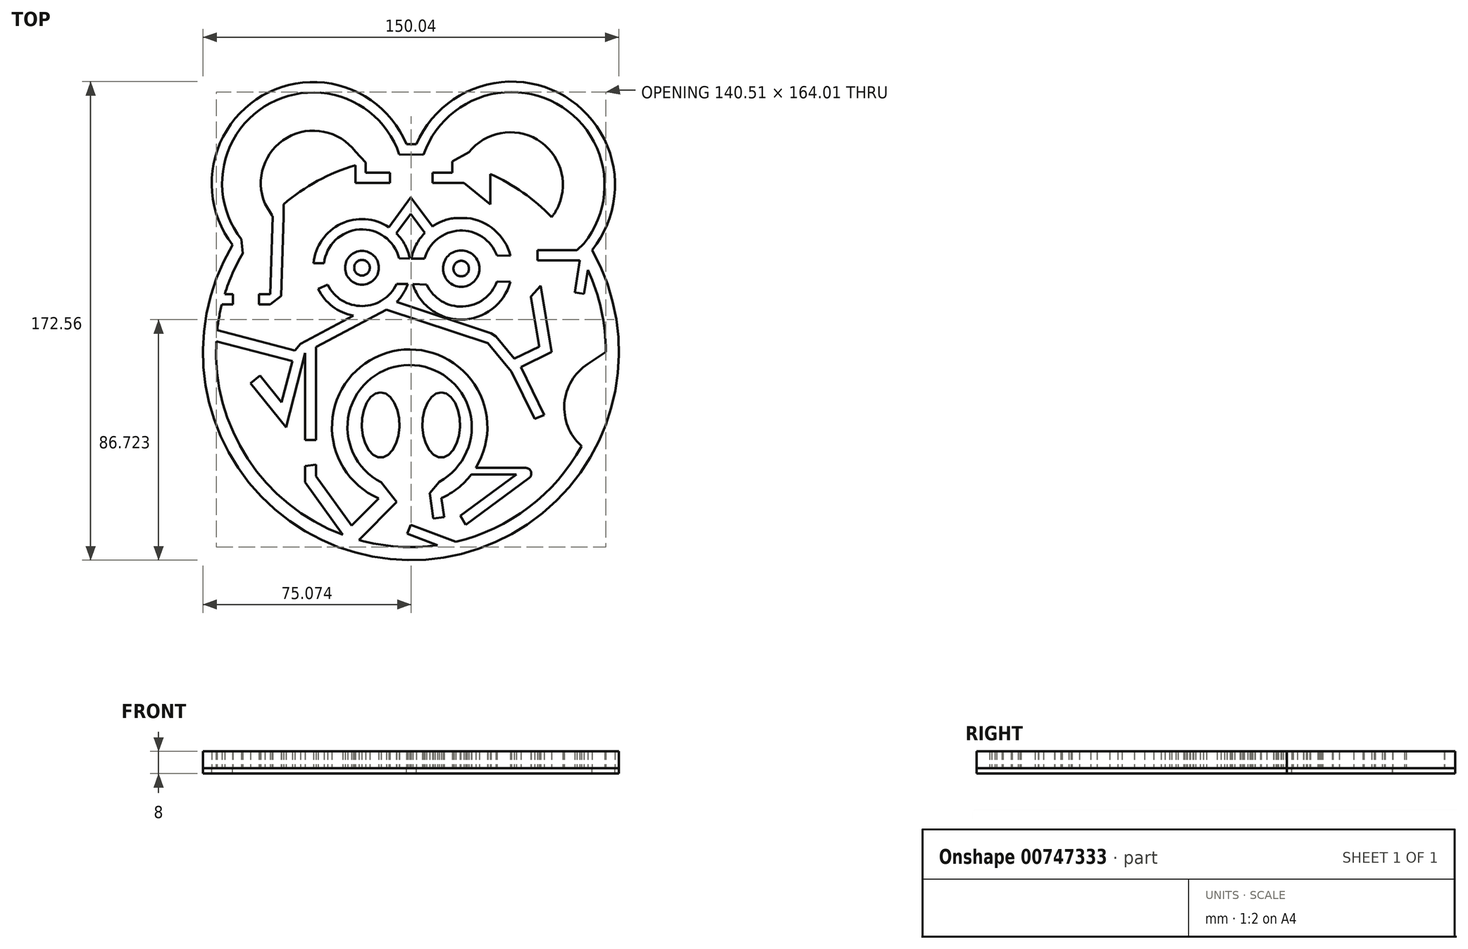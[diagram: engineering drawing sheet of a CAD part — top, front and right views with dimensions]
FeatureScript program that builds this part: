
annotation { "Feature Type Name" : "Feature", "Feature Type Description" : "" }
export const myFeature = defineFeature(function(context is Context, id is Id, definition is map)
    precondition{}
    {
        {
            var Q0;
            Q0=qCreatedBy(makeId("Top.planeOp"),FACE);
            var sketch = newSketch(context, id + "F0", { "sketchPlane" : qUnion([Q0])});
            skArc(sketch, "E0", {"start": v(-64.31, 38.62) * mm, "mid": v(-1.05, -75) * mm, "end": v(65.36, 36.81) * mm});
            skArc(sketch, "E1.0", {"start": v(-68.18, 17.17) * mm, "mid": v(-69.18, 12.55) * mm, "end": v(-69.87, 7.88) * mm});
            skArc(sketch, "E2", {"start": v(-50.1, 94.24) * mm, "mid": v(-70.69, 69.88) * mm, "end": v(-64.31, 38.62) * mm});
            skArc(sketch, "E3", {"start": v(-50.1, 94.24) * mm, "mid": v(-21.8, 94.8) * mm, "end": v(-1.58, 75) * mm});
            skArc(sketch, "E4", {"start": v(53.87, 93.14) * mm, "mid": v(72.86, 67.68) * mm, "end": v(65.36, 36.81) * mm});
            skArc(sketch, "E5", {"start": v(53.87, 93.14) * mm, "mid": v(23.96, 95.45) * mm, "end": v(2.02, 74.99) * mm});
            skArc(sketch, "E6.0", {"start": v(10.18, -46.8) * mm, "mid": v(-0.63, -4.68) * mm, "end": v(-10.76, -46.97) * mm});
            skArc(sketch, "E7.0", {"start": v(53.27, 52.82) * mm, "mid": v(52.03, 50.46) * mm, "end": v(50.46, 48.3) * mm});
            skArc(sketch, "E8", {"start": v(-30, 24.26) * mm, "mid": v(-17.5, 16.6) * mm, "end": v(-5.15, 24.5) * mm});
            skArc(sketch, "E9", {"start": v(5.71, 24.34) * mm, "mid": v(18.76, 16.41) * mm, "end": v(31.05, 25.48) * mm});
            skCircle(sketch, "E10", {"center": v(-17.64, 30.41) * mm, "radius": 6.08 * mm});
            skCircle(sketch, "E11", {"center": v(18.15, 30.11) * mm, "radius": 6.56 * mm});
            skLineSegment(sketch, "E12.trimOffspring", {"start": v(-49.84, 48.88) * mm, "end": v(-50.05, 49.39) * mm, "construction": true});
            skLineSegment(sketch, "E13.trimOffspring", {"start": v(50.46, 48.3) * mm, "end": v(50.66, 48.76) * mm, "construction": true});
            skArc(sketch, "E14.0", {"start": v(-5.2, 18.03) * mm, "mid": v(-2.8, 21.04) * mm, "end": v(-1.1, 24.5) * mm});
            skArc(sketch, "E15.0", {"start": v(15.62, 48.31) * mm, "mid": v(5.54, 43.48) * mm, "end": v(0.12, 33.71) * mm});
            skCircle(sketch, "E16.0", {"center": v(18.15, 30.11) * mm, "radius": 2.81 * mm});
            skCircle(sketch, "E17.0", {"center": v(-17.64, 30.41) * mm, "radius": 2.81 * mm});
            skEllipse(sketch, "E18", {"center": v(-10.95, -26.25) * mm, "majorRadius": 11.74 * mm, "minorRadius": 6.8 * mm, "majorAxis": v(0, 1)});
            skEllipse(sketch, "E19.MirrorC", {"center": v(10.95, -26.25) * mm, "majorRadius": 11.74 * mm, "minorRadius": 6.8 * mm, "majorAxis": v(0, 1)});
            skArc(sketch, "E20.0", {"start": v(11.04, -52.64) * mm, "mid": v(16.92, -49.08) * mm, "end": v(21.75, -44.2) * mm});
            skFitSpline(sketch, "E21.0", {"points": [v(-10.29, -16.58) * mm, v(-10.95, -16.47) * mm, v(-11.6, -16.58) * mm, v(-12.24, -16.9) * mm, v(-12.79, -17.34) * mm, v(-13.35, -17.92) * mm, v(-14.04, -18.89) * mm, v(-14.76, -20.4) * mm, v(-15.31, -22.2) * mm, v(-15.6, -23.84) * mm, v(-15.72, -25.2) * mm, v(-15.75, -26.25) * mm, v(-15.72, -27.3) * mm, v(-15.6, -28.66) * mm, v(-15.31, -30.3) * mm, v(-14.76, -32.1) * mm, v(-14.04, -33.61) * mm, v(-13.35, -34.58) * mm, v(-12.79, -35.16) * mm, v(-12.24, -35.6) * mm, v(-11.6, -35.92) * mm, v(-10.95, -36.03) * mm, v(-10.29, -35.92) * mm, v(-9.65, -35.6) * mm, v(-9.1, -35.16) * mm, v(-8.54, -34.58) * mm, v(-7.85, -33.61) * mm, v(-7.14, -32.1) * mm, v(-6.58, -30.3) * mm, v(-6.29, -28.66) * mm, v(-6.17, -27.3) * mm, v(-6.14, -26.25) * mm, v(-6.17, -25.2) * mm, v(-6.29, -23.84) * mm, v(-6.58, -22.2) * mm, v(-7.14, -20.4) * mm, v(-7.85, -18.89) * mm, v(-8.54, -17.92) * mm, v(-9.1, -17.34) * mm, v(-9.65, -16.9) * mm, v(-10.29, -16.58) * mm, v(-10.95, -16.47) * mm, v(-11.6, -16.58) * mm, v(-10.29, -16.58) * mm]});
            skFitSpline(sketch, "E22.0", {"points": [v(11.6, -16.58) * mm, v(10.95, -16.47) * mm, v(10.29, -16.58) * mm, v(9.65, -16.9) * mm, v(9.1, -17.34) * mm, v(8.54, -17.92) * mm, v(7.85, -18.89) * mm, v(7.14, -20.4) * mm, v(6.58, -22.2) * mm, v(6.29, -23.84) * mm, v(6.17, -25.2) * mm, v(6.14, -26.25) * mm, v(6.17, -27.3) * mm, v(6.29, -28.66) * mm, v(6.58, -30.3) * mm, v(7.14, -32.1) * mm, v(7.85, -33.61) * mm, v(8.54, -34.58) * mm, v(9.1, -35.16) * mm, v(9.65, -35.6) * mm, v(10.29, -35.92) * mm, v(10.95, -36.03) * mm, v(11.6, -35.92) * mm, v(12.24, -35.6) * mm, v(12.79, -35.16) * mm, v(13.35, -34.58) * mm, v(14.04, -33.61) * mm, v(14.76, -32.1) * mm, v(15.31, -30.3) * mm, v(15.6, -28.66) * mm, v(15.72, -27.3) * mm, v(15.75, -26.25) * mm, v(15.72, -25.2) * mm, v(15.6, -23.84) * mm, v(15.31, -22.2) * mm, v(14.76, -20.4) * mm, v(14.04, -18.89) * mm, v(13.35, -17.92) * mm, v(12.79, -17.34) * mm, v(12.24, -16.9) * mm, v(11.6, -16.58) * mm, v(10.95, -16.47) * mm, v(10.29, -16.58) * mm, v(11.6, -16.58) * mm]});
            skLineSegment(sketch, "E23.bottom", {"start": v(10.1, -46.8) * mm, "end": v(10.18, -46.8) * mm, "construction": true});
            skLineSegment(sketch, "E24", {"start": v(-69.87, 7.88) * mm, "end": v(-41.79, 0.6) * mm});
            skLineSegment(sketch, "E25", {"start": v(-38.15, -0.33) * mm, "end": v(-45.08, -27.08) * mm});
            skLineSegment(sketch, "E26", {"start": v(-45.08, -27.08) * mm, "end": v(-57.79, -11.22) * mm});
            skLineSegment(sketch, "E27", {"start": v(-38.15, -46.97) * mm, "end": v(-38.15, -41.04) * mm});
            skLineSegment(sketch, "E28", {"start": v(-38.15, -46.97) * mm, "end": v(-24.58, -65.87) * mm});
            skLineSegment(sketch, "E29", {"start": v(-21.35, -62.6) * mm, "end": v(-11.67, -52.77) * mm});
            skLineSegment(sketch, "E30", {"start": v(-67.14, 20.87) * mm, "end": v(-64.16, 20.87) * mm});
            skLineSegment(sketch, "E31", {"start": v(-50.77, 20.87) * mm, "end": v(-49.84, 48.88) * mm});
            skLineSegment(sketch, "E32", {"start": v(15.62, 48.31) * mm, "end": v(20.3, 48.36) * mm});
            skLineSegment(sketch, "E33", {"start": v(50.81, 0) * mm, "end": v(39.66, -5.46) * mm});
            skLineSegment(sketch, "E34", {"start": v(36.3, -7.11) * mm, "end": v(27.77, 3.17) * mm});
            skLineSegment(sketch, "E35", {"start": v(27.77, 3.17) * mm, "end": v(16.64, 6.84) * mm});
            skLineSegment(sketch, "E36", {"start": v(-8.8, 15.25) * mm, "end": v(-34.18, 1.78) * mm});
            skLineSegment(sketch, "E37", {"start": v(36.3, -7.11) * mm, "end": v(44.6, -24.08) * mm});
            skLineSegment(sketch, "E38", {"start": v(23.4, -41.79) * mm, "end": v(41.4, -41.79) * mm});
            skLineSegment(sketch, "E39", {"start": v(38, -44.18) * mm, "end": v(27.01, -52.25) * mm});
            skLineSegment(sketch, "E40", {"start": v(11.04, -52.64) * mm, "end": v(11.99, -59.47) * mm});
            skLineSegment(sketch, "E41.0", {"start": v(-46.83, 20.25) * mm, "end": v(-45.89, 48.85) * mm});
            skLineSegment(sketch, "E42.0", {"start": v(-70.76, 4.05) * mm, "end": v(-42.77, -3.2) * mm});
            skLineSegment(sketch, "E43.0", {"start": v(-46.65, -18.17) * mm, "end": v(-54.4, -8.5) * mm});
            skLineSegment(sketch, "E44.0", {"start": v(-42.77, -3.2) * mm, "end": v(-46.65, -18.17) * mm});
            skLineSegment(sketch, "E45.0", {"start": v(-34.18, -44.73) * mm, "end": v(-34.18, -40.57) * mm});
            skLineSegment(sketch, "E46.0", {"start": v(-18.7, -67.78) * mm, "end": v(-5.16, -54.03) * mm});
            skLineSegment(sketch, "E47.0", {"start": v(6.84, -50.86) * mm, "end": v(8.1, -60) * mm});
            skLineSegment(sketch, "E48.0", {"start": v(42.6, -45.44) * mm, "end": v(29.24, -55.28) * mm});
            skLineSegment(sketch, "E49.0", {"start": v(28.94, 6.75) * mm, "end": v(18.03, 10.36) * mm});
            skLineSegment(sketch, "E50.0", {"start": v(-10.5, 18.57) * mm, "end": v(-11.68, 17.95) * mm});
            skLineSegment(sketch, "E51.0", {"start": v(37.34, -2.43) * mm, "end": v(30.68, 5.6) * mm});
            skLineSegment(sketch, "E52.0", {"start": v(39.66, -5.46) * mm, "end": v(48.07, -22.63) * mm});
            skLineSegment(sketch, "E53.0", {"start": v(46.35, 1.99) * mm, "end": v(37.34, -2.43) * mm});
            skLineSegment(sketch, "E54.0", {"start": v(-34.18, -44.73) * mm, "end": v(-21.35, -62.6) * mm});
            skLineSegment(sketch, "E55.bottom", {"start": v(-38.15, -31.67) * mm, "end": v(-34.18, -31.67) * mm});
            skLineSegment(sketch, "E56.trimOffspring", {"start": v(-34.18, -31.67) * mm, "end": v(-34.18, -0.33) * mm});
            skLineSegment(sketch, "E57.trimOffspring", {"start": v(-38.15, -31.67) * mm, "end": v(-38.15, -0.33) * mm});
            skLineSegment(sketch, "E58", {"start": v(-38.15, -41.04) * mm, "end": v(-34.18, -40.57) * mm});
            skLineSegment(sketch, "E59", {"start": v(-57.79, -11.22) * mm, "end": v(-54.4, -8.5) * mm});
            skLineSegment(sketch, "E60", {"start": v(-50.75, 17.17) * mm, "end": v(-46.83, 20.25) * mm});
            skLineSegment(sketch, "E61", {"start": v(44.6, -24.08) * mm, "end": v(48.07, -22.63) * mm});
            skLineSegment(sketch, "E62", {"start": v(-39.87, 2.99) * mm, "end": v(-41.79, 0.6) * mm});
            skLineSegment(sketch, "E63", {"start": v(-5.16, -54.03) * mm, "end": v(-10.76, -46.97) * mm});
            skLineSegment(sketch, "E64", {"start": v(61.57, -33.95) * mm, "end": v(61.4, -33.78) * mm});
            skLineSegment(sketch, "E65", {"start": v(63.8, -4.27) * mm, "end": v(70.31, 0) * mm});
            skLineSegment(sketch, "E66", {"start": v(30.68, 5.6) * mm, "end": v(28.94, 6.75) * mm});
            skLineSegment(sketch, "E67", {"start": v(8.1, -60) * mm, "end": v(11.99, -59.47) * mm});
            skLineSegment(sketch, "E68", {"start": v(-34.18, -0.33) * mm, "end": v(-34.18, 1.78) * mm});
            skLineSegment(sketch, "E69", {"start": v(-45.89, 48.85) * mm, "end": v(-45.89, 53.27) * mm});
            skArc(sketch, "E70.trimOffspring", {"start": v(-50.16, 49.27) * mm, "mid": v(-50, 49.07) * mm, "end": v(-49.84, 48.88) * mm});
            skLineSegment(sketch, "E71", {"start": v(-20, 67.4) * mm, "end": v(-20, 60.97) * mm});
            skLineSegment(sketch, "E72", {"start": v(-20.13, 60.97) * mm, "end": v(-20, 60.97) * mm});
            skLineSegment(sketch, "E73", {"start": v(-20, 60.97) * mm, "end": v(-7.59, 60.97) * mm});
            skLineSegment(sketch, "E74.0", {"start": v(-16.3, 67.4) * mm, "end": v(-16.3, 64.7) * mm});
            skLineSegment(sketch, "E75.0", {"start": v(-16.3, 64.7) * mm, "end": v(-7.59, 64.7) * mm});
            skLineSegment(sketch, "E76.0", {"start": v(14.9, 67.25) * mm, "end": v(14.9, 64.7) * mm});
            skLineSegment(sketch, "E77", {"start": v(-16.3, 67.4) * mm, "end": v(-16.3, 68.4) * mm});
            skLineSegment(sketch, "E78", {"start": v(14.9, 67.25) * mm, "end": v(14.9, 68.72) * mm});
            skLineSegment(sketch, "E79", {"start": v(-52.62, 53.47) * mm, "end": v(-50.16, 49.27) * mm});
            skLineSegment(sketch, "E80", {"start": v(-50.75, 17.17) * mm, "end": v(-54.78, 17.17) * mm});
            skLineSegment(sketch, "E81.left", {"start": v(-64.16, 20.87) * mm, "end": v(-64.16, 17.17) * mm});
            skLineSegment(sketch, "E81.right", {"start": v(-54.78, 20.87) * mm, "end": v(-54.78, 17.17) * mm});
            skLineSegment(sketch, "E82.trimOffspring", {"start": v(-54.78, 20.87) * mm, "end": v(-50.77, 20.87) * mm});
            skLineSegment(sketch, "E83.trimOffspring", {"start": v(-64.16, 17.17) * mm, "end": v(-68.18, 17.17) * mm});
            skArc(sketch, "E84.trimOffspring", {"start": v(-20, 67.4) * mm, "mid": v(-33.7, 61.71) * mm, "end": v(-45.89, 53.27) * mm});
            skArc(sketch, "E85.trimOffspring", {"start": v(2.02, 74.99) * mm, "mid": v(0.22, 75.02) * mm, "end": v(-1.58, 75) * mm});
            skLineSegment(sketch, "E86", {"start": v(-20, 72.3) * mm, "end": v(-16.3, 68.4) * mm});
            skLineSegment(sketch, "E87", {"start": v(14.9, 68.72) * mm, "end": v(20.93, 72.04) * mm});
            skLineSegment(sketch, "E88.left", {"start": v(-7.59, 64.7) * mm, "end": v(-7.59, 60.97) * mm});
            skLineSegment(sketch, "E88.right", {"start": v(7.76, 64.7) * mm, "end": v(7.76, 60.97) * mm});
            skLineSegment(sketch, "E89.trimOffspring", {"start": v(7.76, 60.97) * mm, "end": v(19.1, 60.97) * mm});
            skLineSegment(sketch, "E90.trimOffspring", {"start": v(7.76, 64.7) * mm, "end": v(14.9, 64.7) * mm});
            skArc(sketch, "E91.trimOffspring", {"start": v(50.66, 48.76) * mm, "mid": v(40.4, 57.55) * mm, "end": v(28.64, 64.22) * mm});
            skLineSegment(sketch, "E92", {"start": v(60.93, 33.06) * mm, "end": v(59.15, 21.47) * mm});
            skLineSegment(sketch, "E93", {"start": v(59.93, 36.81) * mm, "end": v(45.66, 36.81) * mm});
            skLineSegment(sketch, "E94", {"start": v(59.93, 36.81) * mm, "end": v(59.83, 36.98) * mm});
            skLineSegment(sketch, "E95.0", {"start": v(60.93, 33.06) * mm, "end": v(45.66, 33.06) * mm});
            skLineSegment(sketch, "E96.0", {"start": v(63.78, 29.6) * mm, "end": v(62.45, 20.97) * mm});
            skLineSegment(sketch, "E97", {"start": v(45.66, 36.81) * mm, "end": v(45.66, 33.06) * mm});
            skLineSegment(sketch, "E98", {"start": v(59.15, 21.47) * mm, "end": v(62.45, 20.97) * mm});
            skLineSegment(sketch, "E99", {"start": v(50.81, 0) * mm, "end": v(46.74, 23.86) * mm});
            skLineSegment(sketch, "E100.0", {"start": v(46.35, 1.99) * mm, "end": v(43.29, 19.94) * mm});
            skArc(sketch, "E101.trimOffspring", {"start": v(70.31, 0) * mm, "mid": v(68.66, 15.16) * mm, "end": v(63.78, 29.6) * mm});
            skArc(sketch, "E102.trimOffspring", {"start": v(-18.7, -67.78) * mm, "mid": v(27.3, -64.8) * mm, "end": v(61.57, -33.95) * mm});
            skArc(sketch, "E103.trimOffspring", {"start": v(-70.2, 3.9) * mm, "mid": v(-58.85, -38.48) * mm, "end": v(-24.58, -65.87) * mm});
            skArc(sketch, "E104.trimOffspring", {"start": v(-60.62, 35.61) * mm, "mid": v(0.7, -70.3) * mm, "end": v(59.9, 36.81) * mm});
            skLineSegment(sketch, "E105.trimOffspring", {"start": v(-20.74, 13.14) * mm, "end": v(-39.87, 2.99) * mm});
            skLineSegment(sketch, "E106", {"start": v(43.29, 19.94) * mm, "end": v(46.74, 23.86) * mm});
            skLineSegment(sketch, "E107", {"start": v(-7.97, 45.07) * mm, "end": v(0, 55.75) * mm});
            skLineSegment(sketch, "E108.MirrorCS", {"start": v(7.8, 45.3) * mm, "end": v(0, 55.75) * mm});
            skLineSegment(sketch, "E109.0", {"start": v(-5.06, 43.05) * mm, "end": v(-0.05, 49.78) * mm});
            skLineSegment(sketch, "E110.0", {"start": v(4.73, 43.37) * mm, "end": v(-0.05, 49.78) * mm});
            skLineSegment(sketch, "E111", {"start": v(19.1, 60.97) * mm, "end": v(29.27, 52.79) * mm});
            skLineSegment(sketch, "E112", {"start": v(28.64, 52.83) * mm, "end": v(28.64, 64.22) * mm});
            skPoint(sketch, "E113.visualSharp", {"position": v(43.6, -17.48) * mm});
            skArc(sketch, "E113.filletArc", {"start": v(63.8, -4.27) * mm, "mid": v(55.37, -18.44) * mm, "end": v(61.4, -33.78) * mm});
            skArc(sketch, "E114.filletArc", {"start": v(42.6, -45.44) * mm, "mid": v(43.33, -43.18) * mm, "end": v(41.4, -41.79) * mm});
            skLineSegment(sketch, "E115", {"start": v(21.95, -44.18) * mm, "end": v(21.75, -44.2) * mm});
            skArc(sketch, "E116.trimOffspring", {"start": v(23.4, -41.79) * mm, "mid": v(-8.82, -0.33) * mm, "end": v(-11.67, -52.77) * mm});
            skLineSegment(sketch, "E117", {"start": v(29.24, -55.28) * mm, "end": v(19.71, -62.28) * mm});
            skLineSegment(sketch, "E118", {"start": v(16.18, -68.42) * mm, "end": v(0, -62.28) * mm});
            skLineSegment(sketch, "E119.0", {"start": v(9.64, -69.65) * mm, "end": v(-1.37, -65.46) * mm});
            skArc(sketch, "E120.trimOffspring", {"start": v(-10.04, 14.59) * mm, "mid": v(-9.4, 14.9) * mm, "end": v(-8.8, 15.25) * mm});
            skLineSegment(sketch, "E121", {"start": v(27.01, -52.25) * mm, "end": v(17.82, -59.02) * mm});
            skLineSegment(sketch, "E122", {"start": v(19.71, -62.28) * mm, "end": v(17.82, -59.02) * mm});
            skLineSegment(sketch, "E123", {"start": v(-1.37, -65.46) * mm, "end": v(0, -62.28) * mm});
            skArc(sketch, "E124.trimOffspring", {"start": v(-33.44, 22.77) * mm, "mid": v(-28.25, 16.43) * mm, "end": v(-20.74, 13.14) * mm});
            skArc(sketch, "E125.trimOffspring", {"start": v(0.64, 24.5) * mm, "mid": v(3.73, 18.7) * mm, "end": v(8.66, 14.37) * mm});
            skArc(sketch, "E126.trimOffspring", {"start": v(-0.4, 33.71) * mm, "mid": v(-18.45, 47.95) * mm, "end": v(-35.1, 32.11) * mm});
            skArc(sketch, "E127.trimOffspring", {"start": v(35.94, 34.71) * mm, "mid": v(30.23, 43.96) * mm, "end": v(20.3, 48.36) * mm});
            skArc(sketch, "E128.trimOffspring", {"start": v(18.03, 11.73) * mm, "mid": v(29.28, 15.48) * mm, "end": v(35.89, 25.32) * mm});
            skLineSegment(sketch, "E129.trimOffspring", {"start": v(8.66, 13.46) * mm, "end": v(-5.2, 18.03) * mm});
            skLineSegment(sketch, "E130.trimOffspring", {"start": v(8.66, 9.48) * mm, "end": v(-8.8, 15.25) * mm});
            skLineSegment(sketch, "E131", {"start": v(18, 10.49) * mm, "end": v(17.96, 10.38) * mm});
            skLineSegment(sketch, "E132", {"start": v(-35.1, 32.11) * mm, "end": v(-31.36, 31.99) * mm});
            skLineSegment(sketch, "E133", {"start": v(-0.4, 33.71) * mm, "end": v(-4.25, 33.84) * mm});
            skLineSegment(sketch, "E134", {"start": v(-1.1, 24.5) * mm, "end": v(-5.15, 24.5) * mm});
            skLineSegment(sketch, "E135", {"start": v(0.64, 24.5) * mm, "end": v(5.71, 24.34) * mm});
            skLineSegment(sketch, "E136", {"start": v(0.12, 33.71) * mm, "end": v(4.92, 33.71) * mm});
            skLineSegment(sketch, "E137", {"start": v(35.94, 34.71) * mm, "end": v(31, 34.87) * mm});
            skLineSegment(sketch, "E138", {"start": v(35.89, 25.32) * mm, "end": v(31.05, 25.48) * mm});
            skLineSegment(sketch, "E139", {"start": v(-33.44, 22.77) * mm, "end": v(-30, 24.26) * mm});
            skArc(sketch, "E140.trimOffspring", {"start": v(-4.25, 33.84) * mm, "mid": v(-18.58, 44.2) * mm, "end": v(-31.36, 31.99) * mm});
            skArc(sketch, "E141.trimOffspring", {"start": v(31, 34.87) * mm, "mid": v(17.54, 43.8) * mm, "end": v(4.92, 33.71) * mm});
            skArc(sketch, "E142.trimOffspring", {"start": v(50.76, 48.65) * mm, "mid": v(40.45, 57.5) * mm, "end": v(28.64, 64.22) * mm});
            skLineSegment(sketch, "E143", {"start": v(-5.06, 43.05) * mm, "end": v(-5.23, 42.83) * mm});
            skLineSegment(sketch, "E144", {"start": v(4.73, 43.37) * mm, "end": v(5.03, 42.98) * mm});
            skArc(sketch, "E145", {"start": v(8.66, 14.37) * mm, "mid": v(13.15, 12.35) * mm, "end": v(18.03, 11.73) * mm});
            skLineSegment(sketch, "E146", {"start": v(8.66, 9.48) * mm, "end": v(16.64, 6.84) * mm});
            skLineSegment(sketch, "E147", {"start": v(18.03, 10.36) * mm, "end": v(8.66, 13.46) * mm});
            skArc(sketch, "E148", {"start": v(-20, 72.3) * mm, "mid": v(-44.64, 77.3) * mm, "end": v(-52.62, 53.47) * mm});
            skArc(sketch, "E149", {"start": v(53.27, 52.82) * mm, "mid": v(45.53, 76.62) * mm, "end": v(20.93, 72.04) * mm});
            skArc(sketch, "E150.0", {"start": v(-48.57, 90.8) * mm, "mid": v(-22.08, 90.86) * mm, "end": v(-4.19, 71.3) * mm});
            skArc(sketch, "E151.0", {"start": v(-48.57, 90.8) * mm, "mid": v(-67.1, 68.8) * mm, "end": v(-61.16, 40.67) * mm});
            skLineSegment(sketch, "E152", {"start": v(-61.16, 40.67) * mm, "end": v(-60.62, 35.61) * mm});
            skArc(sketch, "E153.0", {"start": v(52.1, 89.84) * mm, "mid": v(24.05, 91.48) * mm, "end": v(4.58, 71.23) * mm});
            skArc(sketch, "E154.0", {"start": v(52.1, 89.84) * mm, "mid": v(69.19, 66.93) * mm, "end": v(62.44, 39.16) * mm});
            skLineSegment(sketch, "E155", {"start": v(62.44, 39.16) * mm, "end": v(59.93, 36.81) * mm});
            skLineSegment(sketch, "E156", {"start": v(-4.19, 71.3) * mm, "end": v(4.58, 71.23) * mm});
            skLineSegment(sketch, "E157", {"start": v(6.84, -50.86) * mm, "end": v(10.18, -46.8) * mm});
            skLineSegment(sketch, "E158", {"start": v(21.95, -44.18) * mm, "end": v(38, -44.18) * mm});
            skSolve(sketch);
        }
        {
            var Q0;
            Q0 = qSketchRegion(id + "F0", true);
            var Q1;
            Q1=makeQuery(id+"F0.imprint","IMPRINT",FACE,{"disambiguationData":[TD([[makeQuery(id+"F0.imprint","IMPRINT",EDGE,{"derivedFrom":sQuery(id+"F0.wireOp",EDGE,"E6.0")}),-1.0]])]});
            var Q2;
            {var subQ0=sQuery(id+"F0.wireOp",EDGE,"E118");Q2=makeQuery(id+"F0.imprint","IMPRINT",FACE,{"disambiguationData":[TD([[makeQuery(id+"F0.imprint","IMPRINT",EDGE,{"derivedFrom":subQ0}),1.0]])]});}
            var Q3;
            Q3=makeQuery(id+"F0.imprint","IMPRINT",FACE,{"disambiguationData":[TD([[makeQuery(id+"F0.imprint","IMPRINT",EDGE,{"derivedFrom":sQuery(id+"F0.wireOp",EDGE,"E18")}),1.0]])]});
            var Q4;
            Q4=makeQuery(id+"F0.imprint","IMPRINT",FACE,{"disambiguationData":[TD([[makeQuery(id+"F0.imprint","IMPRINT",EDGE,{"derivedFrom":sQuery(id+"F0.wireOp",EDGE,"E19.MirrorC")}),1.0]])]});
            var Q5;
            Q5=makeQuery(id+"F0.imprint","IMPRINT",FACE,{"disambiguationData":[TD([[makeQuery(id+"F0.imprint","IMPRINT",EDGE,{"derivedFrom":sQuery(id+"F0.wireOp",EDGE,"E31")}),-1.0]])]});
            var Q6;
            Q6=makeQuery(id+"F0.imprint","IMPRINT",FACE,{"disambiguationData":[TD([[makeQuery(id+"F0.imprint","IMPRINT",EDGE,{"derivedFrom":sQuery(id+"F0.wireOp",EDGE,"E76.0")}),1.0]])]});
            var Q7;
            {var subQ1=sQuery(id+"F0.wireOp",EDGE,"E107");Q7=makeQuery(id+"F0.imprint","IMPRINT",FACE,{"disambiguationData":[TD([[makeQuery(id+"F0.imprint","IMPRINT",EDGE,{"derivedFrom":subQ1}),-1.0]])]});}
            var Q8;
            {var subQ0=sQuery(id+"F0.wireOp",EDGE,"E32");Q8=makeQuery(id+"F0.imprint","IMPRINT",FACE,{"disambiguationData":[TD([[makeQuery(id+"F0.imprint","IMPRINT",EDGE,{"derivedFrom":subQ0}),-1.0]])]});}
            var Q9;
            {var subQ0=sQuery(id+"F0.wireOp",EDGE,"E132");Q9=makeQuery(id+"F0.imprint","IMPRINT",FACE,{"disambiguationData":[TD([[makeQuery(id+"F0.imprint","IMPRINT",EDGE,{"derivedFrom":subQ0}),1.0]])]});}
            var Q10;
            Q10=makeQuery(id+"F0.imprint","IMPRINT",FACE,{"disambiguationData":[TD([[makeQuery(id+"F0.imprint","IMPRINT",EDGE,{"derivedFrom":sQuery(id+"F0.wireOp",EDGE,"E14.0")}),1.0]])]});
            var Q11;
            Q11=makeQuery(id+"F0.imprint","IMPRINT",FACE,{"disambiguationData":[TD([[makeQuery(id+"F0.imprint","IMPRINT",EDGE,{"derivedFrom":sQuery(id+"F0.wireOp",EDGE,"E9")}),-1.0]])]});
            var Q12;
            {var subQ0=sQuery(id+"F0.wireOp",EDGE,"E64");Q12=makeQuery(id+"F0.imprint","IMPRINT",FACE,{"disambiguationData":[TD([[makeQuery(id+"F0.imprint","IMPRINT",EDGE,{"derivedFrom":subQ0}),-1.0]])]});}
            var Q13;
            Q13=makeQuery(id+"F0.imprint","IMPRINT",FACE,{"disambiguationData":[TD([[makeQuery(id+"F0.imprint","IMPRINT",EDGE,{"derivedFrom":sQuery(id+"F0.wireOp",EDGE,"E92")}),1.0]])]});
            var Q14;
            {var subQ0=sQuery(id+"F0.wireOp",EDGE,"E30");Q14=makeQuery(id+"F0.imprint","IMPRINT",FACE,{"disambiguationData":[TD([[makeQuery(id+"F0.imprint","IMPRINT",EDGE,{"derivedFrom":subQ0}),-1.0]])]});}
            var Q15;
            Q15=makeQuery(id+"F0.imprint","IMPRINT",FACE,{"disambiguationData":[TD([[makeQuery(id+"F0.imprint","IMPRINT",EDGE,{"derivedFrom":sQuery(id+"F0.wireOp",EDGE,"E10")}),1.0]])]});
            var Q16;
            Q16=makeQuery(id+"F0.imprint","IMPRINT",FACE,{"disambiguationData":[TD([[makeQuery(id+"F0.imprint","IMPRINT",EDGE,{"derivedFrom":sQuery(id+"F0.wireOp",EDGE,"E11")}),1.0]])]});
            extrude(context, id + "F1", {"entities" : qUnion([Q0, Q1, Q2, Q3, Q4, Q5, Q6, Q7, Q8, Q9, Q10, Q11, Q12, Q13, Q14, Q15, Q16]), "depth" : 6 * mm, "offsetDistance" : 25 * mm});
        }
        {
            var Q0;
            Q0=qCreatedBy(makeId("Top.planeOp"),FACE);
            var sketch = newSketch(context, id + "F2", { "sketchPlane" : qUnion([Q0])});
            skPoint(sketch, "E159.0.end.orphan", {"position": v(-1.58, 75) * mm});
            skPoint(sketch, "E159.0.start.orphan", {"position": v(2.02, 74.99) * mm});
            skPoint(sketch, "E160.0.end.orphan", {"position": v(65.36, 36.81) * mm});
            skPoint(sketch, "E160.0.start.orphan", {"position": v(-64.31, 38.62) * mm});
            skArc(sketch, "E161.0", {"start": v(65.36, 36.81) * mm, "mid": v(55.56, 92.19) * mm, "end": v(2.02, 74.99) * mm});
            skPoint(sketch, "E162.0", {"position": v(0.22, 75.02) * mm});
            skArc(sketch, "E163.0", {"start": v(2.02, 74.99) * mm, "mid": v(0.22, 75.02) * mm, "end": v(-1.58, 75) * mm});
            skArc(sketch, "E164.0", {"start": v(-64.31, 38.62) * mm, "mid": v(-53.61, 92.45) * mm, "end": v(-1.58, 75) * mm});
            skArc(sketch, "E165.0", {"start": v(-64.31, 38.62) * mm, "mid": v(-1.05, -75) * mm, "end": v(65.36, 36.81) * mm});
            skSolve(sketch);
        }
        {
            var Q0;
            Q0 = qSketchRegion(id + "F2", true);
            extrude(context, id + "F3", {"entities" : qUnion([Q0]), "oppositeDirection" : true, "depth" : 2 * mm, "offsetDistance" : 25 * mm});
        }
    });
